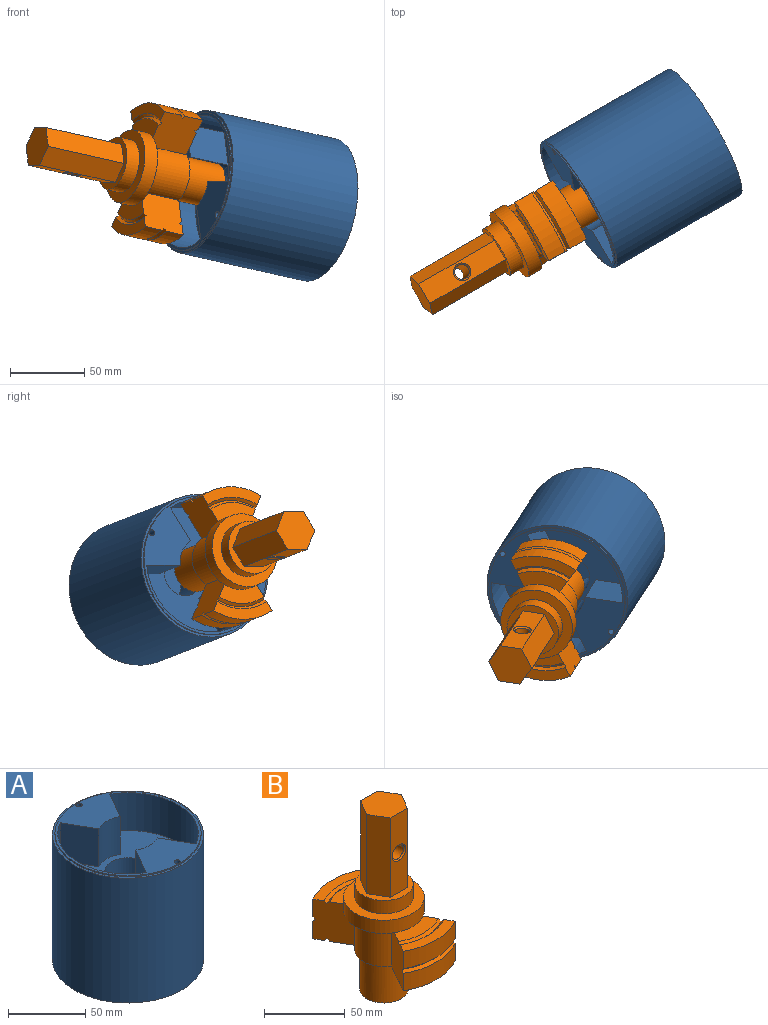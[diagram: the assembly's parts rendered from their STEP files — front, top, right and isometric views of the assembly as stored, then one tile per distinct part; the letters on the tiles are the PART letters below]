
ASSEMBLY  parts=2 mates=1
PART A: 27 faces, bbox 98x98x100 mm
  f0: cylinder r=49mm len=99mm, axis (0,0,1), area 30479.7mm2, adj f1,f3
  f1: plane 98x98mm, normal (0,0,-1), area 6958.4mm2, adj f0,f20,f21,f22,f23,f24,f25
  f2: cylinder r=47.4mm len=94.8mm, axis (0,0,1), area 297.8mm2, adj f3,f4
  f3: plane 98x98mm, normal (0,0,1), area 484.6mm2, adj f0,f2
  f4: plane 94.8x94.8mm, normal (0,0,1), area 2280.1mm2, adj f2,f5,f6,f7,f8,f9,f10,f11
  f5: plane 30x22.6mm, normal (-0.87,-0.5,0), area 783mm2, adj f4,f6,f12,f13
  f6: cylinder r=45.6mm len=78.98mm, axis (0,0,1), area 2865.1mm2, adj f4,f5,f7,f13
  f7: plane 30x22.6mm, normal (-0.87,0.5,0), area 783mm2, adj f4,f6,f8,f13
  f8: cylinder r=19.5mm len=30mm, axis (0,0,1), area 612.6mm2, adj f4,f7,f9,f13
  f9: plane 30x22.6mm, normal (0.87,0.5,0), area 783mm2, adj f4,f8,f10,f13
  f10: cylinder r=45.6mm len=78.98mm, axis (0,0,1), area 2865.1mm2, adj f4,f9,f11,f13
  f11: plane 30x22.6mm, normal (0.87,-0.5,0), area 783mm2, adj f4,f10,f12,f13
  f12: cylinder r=19.5mm len=30mm, axis (0,0,1), area 612.6mm2, adj f4,f5,f11,f13
  f13: plane 91.2x78.98mm, normal (0,0,1), area 4046.3mm2, adj f5,f6,f7,f8,f9,f10,f11,f12
  f14: cylinder r=15mm len=30mm, axis (0,0,1), area 2827.4mm2, adj f13,f15
  f15: plane 30x30mm, normal (0,0,1), area 706.9mm2, adj f14
  f16: cylinder r=2mm len=10mm, axis (0,0,1), area 125.7mm2, adj f4,f17
  f17: plane 4x4mm, normal (0,0,1), area 12.6mm2, adj f16
  f18: cylinder r=2mm len=10mm, axis (0,0,1), area 125.7mm2, adj f4,f19
  f19: plane 4x4mm, normal (0,0,1), area 12.6mm2, adj f18
  f20: plane 30x15mm, normal (-0.02,1,0), area 450mm2, adj f1,f21,f25,f26
  f21: plane 30x12.87mm, normal (0.86,0.51,0), area 450mm2, adj f1,f20,f22,f26
  f22: plane 30x13.11mm, normal (0.87,-0.49,0), area 450mm2, adj f1,f21,f23,f26
  f23: plane 30x15mm, normal (0.02,-1,0), area 450mm2, adj f1,f22,f24,f26
  f24: plane 30x12.87mm, normal (-0.86,-0.51,0), area 450mm2, adj f1,f23,f25,f26
  f25: plane 30x13.11mm, normal (-0.87,0.49,0), area 450mm2, adj f1,f20,f24,f26
  f26: plane 30x26.22mm, normal (0,0,-1), area 584.6mm2, adj f20,f21,f22,f23,f24,f25
PART B: 47 faces, bbox 50x91x139.7 mm
  f0: plane 36x36mm, normal (0,0,1), area 433.3mm2, adj f36,f37,f38,f39,f40,f41,f42
  f1: cylinder r=15mm len=30mm, axis (0,0,1), area 2799.2mm2, adj f2,f5
  f2: plane 30x30mm, normal (0,0,-1), area 706.9mm2, adj f1
  f3: cylinder r=18mm len=31.18mm, axis (0,0,-1), area 1131mm2, adj f5,f17,f19,f34
  f4: cylinder r=18mm len=31.18mm, axis (0,0,-1), area 1131mm2, adj f5,f18,f20,f35
  f5: plane 69.4x36mm, normal (0,0,-1), area 1232.6mm2, adj f1,f3,f4,f15,f17,f18,f19,f20
  f6: cone r=36.5mm half-angle=45deg, axis (0,0,-1), area 94.9mm2, adj f7,f16,f17,f18
  f7: cone r=38.3mm half-angle=45deg, axis (0,0,1), area 99.7mm2, adj f6,f8,f17,f18
  f8: plane 45.5x12.33mm, normal (0,0,1), area 315.9mm2, adj f7,f9,f17,f18
  f9: cylinder r=45.5mm len=45.5mm, axis (0,0,-1), area 628.9mm2, adj f8,f10,f17,f18
  f10: cone r=45.5mm half-angle=45deg, axis (0,0,1), area 118.9mm2, adj f9,f11,f17,f18
  f11: cone r=43.7mm half-angle=45deg, axis (0,0,-1), area 118.9mm2, adj f10,f12,f17,f18
  f12: cylinder r=45.5mm len=45.5mm, axis (0,0,-1), area 628.9mm2, adj f11,f13,f17,f18
  f13: plane 45.5x12.33mm, normal (0,0,-1), area 315.9mm2, adj f12,f14,f17,f18
  f14: cone r=38.3mm half-angle=45deg, axis (0,0,-1), area 99.7mm2, adj f13,f15,f17,f18
  f15: cone r=36.5mm half-angle=45deg, axis (0,0,1), area 94.9mm2, adj f5,f14,f17,f18
  f16: plane 34.7x13.05mm, normal (0,0,1), area 303.2mm2, adj f6,f17,f18,f32
  f17: plane 30x23.82mm, normal (0.87,0.5,0), area 815.3mm2, adj f3,f5,f6,f7,f8,f9,f10,f11
  f18: plane 30x23.82mm, normal (-0.87,0.5,0), area 815.3mm2, adj f4,f5,f6,f7,f8,f9,f10,f11
  f19: plane 30x23.82mm, normal (0.87,-0.5,0), area 815.3mm2, adj f3,f5,f21,f22,f23,f24,f25,f26
  f20: plane 30x23.82mm, normal (-0.87,-0.5,0), area 815.3mm2, adj f4,f5,f21,f22,f23,f24,f25,f26
  f21: cylinder r=45.5mm len=45.5mm, axis (0,0,-1), area 628.9mm2, adj f19,f20,f22,f27
  f22: plane 45.5x12.33mm, normal (0,0,1), area 315.9mm2, adj f19,f20,f21,f28
  f23: plane 45.5x12.33mm, normal (0,0,-1), area 315.9mm2, adj f19,f20,f24,f30
  f24: cylinder r=45.5mm len=45.5mm, axis (0,0,-1), area 628.9mm2, adj f19,f20,f23,f26
  f25: plane 34.7x13.05mm, normal (0,0,1), area 303.2mm2, adj f19,f20,f29,f32
  f26: cone r=43.7mm half-angle=45deg, axis (0,0,-1), area 118.9mm2, adj f19,f20,f24,f27
  f27: cone r=45.5mm half-angle=45deg, axis (0,0,1), area 118.9mm2, adj f19,f20,f21,f26
  f28: cone r=38.3mm half-angle=45deg, axis (0,0,1), area 99.7mm2, adj f19,f20,f22,f29
  f29: cone r=36.5mm half-angle=45deg, axis (0,0,-1), area 94.9mm2, adj f19,f20,f25,f28
  f30: cone r=38.3mm half-angle=45deg, axis (0,0,-1), area 99.7mm2, adj f19,f20,f23,f31
  f31: cone r=36.5mm half-angle=45deg, axis (0,0,1), area 94.9mm2, adj f5,f19,f20,f30
  f32: cylinder r=25mm len=50mm, axis (0,0,-1), area 1570.8mm2, adj f16,f25,f33,f34,f35
  f33: plane 50x50mm, normal (0,0,1), area 945.6mm2, adj f32,f36
  f34: plane 43.3x16mm, normal (0,0,-1), area 315.2mm2, adj f3,f17,f19,f32
  f35: plane 43.3x16mm, normal (0,0,-1), area 315.2mm2, adj f4,f18,f20,f32
  f36: cylinder r=18mm len=36mm, axis (0,0,-1), area 1131mm2, adj f0,f33
  f37: plane 60x15mm, normal (0,-1,0), area 786.9mm2, adj f0,f38,f42,f43,f45
  f38: plane 60x12.99mm, normal (0.87,-0.5,0), area 900mm2, adj f0,f37,f39,f43
  f39: plane 60x12.99mm, normal (0.87,0.5,0), area 900mm2, adj f0,f38,f40,f43
  f40: plane 60x15mm, normal (0,1,0), area 786.9mm2, adj f0,f39,f41,f43,f46
  f41: plane 60x12.99mm, normal (-0.87,0.5,0), area 900mm2, adj f0,f40,f42,f43
  f42: plane 60x12.99mm, normal (-0.87,-0.5,0), area 900mm2, adj f0,f37,f41,f43
  f43: plane 30x25.98mm, normal (0,0,1), area 584.6mm2, adj f37,f38,f39,f40,f41,f42
  f44: cylinder r=5mm len=23.98mm, axis (0,-1,0), area 753.4mm2, adj f45,f46
  f45: cone r=5mm half-angle=45deg, axis (0,-1,0), area 48.9mm2, adj f37,f44
  f46: cone r=6mm half-angle=45deg, axis (0,1,0), area 48.9mm2, adj f40,f44
PLACE A rot(axis=(0.5,-0.87,0),79deg) t=(-22.09,7.98,176.62)mm
PLACE B rot(axis=(0.74,-0.43,-0.52),96.1deg) t=(-33.93,1.15,179.28)mm
MATE cylindrical B.f1 <-> A.f14  axis (0.85,0.49,-0.19) through (-8.68,15.73,173.61)mm
